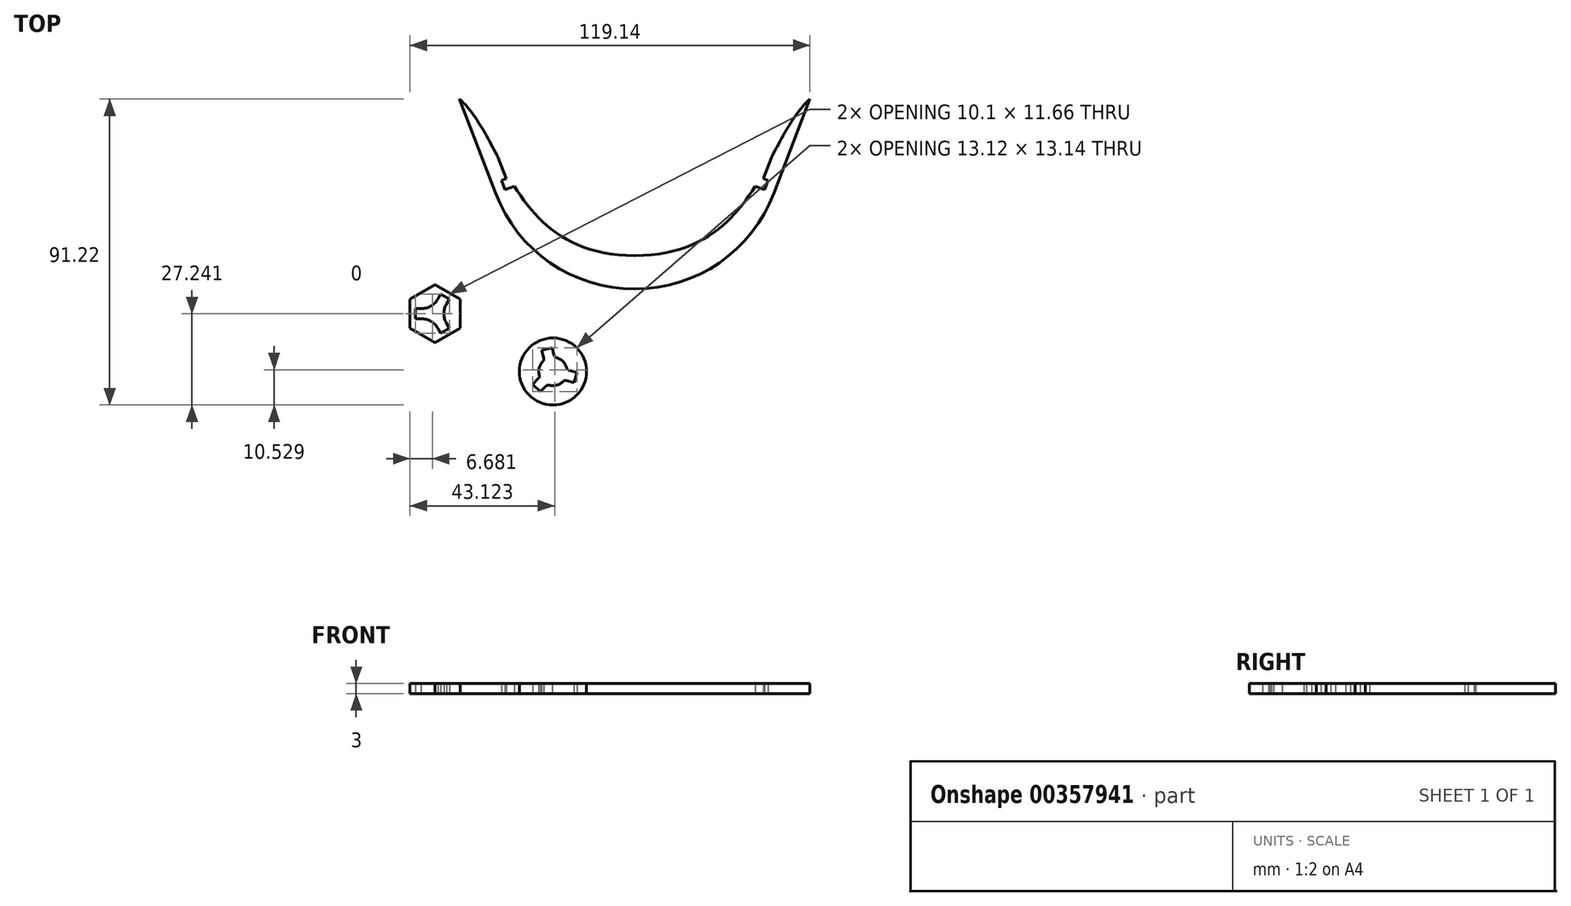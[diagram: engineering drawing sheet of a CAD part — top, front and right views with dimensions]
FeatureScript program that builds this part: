
annotation { "Feature Type Name" : "Feature", "Feature Type Description" : "" }
export const myFeature = defineFeature(function(context is Context, id is Id, definition is map)
    precondition{}
    {
        {
            var Q0;
            Q0=qCreatedBy(makeId("Top.planeOp"),FACE);
            var sketch = newSketch(context, id + "F0", { "sketchPlane" : qUnion([Q0])});
            skLineSegment(sketch, "E0", {"start": v(-52.2, 46.65) * mm, "end": v(0, -90) * mm});
            skLineSegment(sketch, "E1", {"start": v(0, -90) * mm, "end": v(0, -10) * mm});
            skLineSegment(sketch, "E2", {"start": v(-52.2, 46.65) * mm, "end": v(-43.66, 39.02) * mm, "construction": true});
            skLineSegment(sketch, "E3", {"start": v(-41.46, 18.55) * mm, "end": v(-41.46, 18.55) * mm});
            skArc(sketch, "E4", {"start": v(-41.46, 18.55) * mm, "mid": v(-25.17, -2.17) * mm, "end": v(0, -10) * mm});
            skLineSegment(sketch, "E5", {"start": v(0, -10) * mm, "end": v(0, 0) * mm});
            skLineSegment(sketch, "E6", {"start": v(-41.46, 18.55) * mm, "end": v(-36.56, 20.42) * mm, "construction": true});
            skLineSegment(sketch, "E7", {"start": v(-43.66, 39.02) * mm, "end": v(-36.56, 20.42) * mm, "construction": true});
            skLineSegment(sketch, "E8.bottom", {"start": v(-37.26, 20.15) * mm, "end": v(-40.82, 29.5) * mm});
            skLineSegment(sketch, "E8.top", {"start": v(-35.86, 20.69) * mm, "end": v(-39.42, 30.03) * mm});
            skLineSegment(sketch, "E8.left", {"start": v(-37.26, 20.15) * mm, "end": v(-35.86, 20.69) * mm});
            skLineSegment(sketch, "E8.right", {"start": v(-40.82, 29.5) * mm, "end": v(-39.42, 30.03) * mm});
            skPoint(sketch, "E8.middle", {"position": v(-38.34, 25.09) * mm});
            skLineSegment(sketch, "E9", {"start": v(-37.26, 20.15) * mm, "end": v(-38.66, 19.62) * mm});
            skLineSegment(sketch, "E10", {"start": v(-38.66, 19.62) * mm, "end": v(-39.73, 22.42) * mm});
            skLineSegment(sketch, "E11", {"start": v(-39.73, 22.42) * mm, "end": v(-38.33, 22.95) * mm});
            skFitSpline(sketch, "E12", {"points": [v(-52.2, 46.65) * mm, v(0, 0) * mm], "startDerivative": vector(41.8, -37.36) * mm, "endDerivative": vector(109.39, 0) * mm});
            skLineSegment(sketch, "E13", {"start": v(-36.46, 0) * mm, "end": v(0, 0) * mm, "construction": true});
            skLineSegment(sketch, "E14", {"start": v(-38.26, 34.2) * mm, "end": v(0, 0) * mm, "construction": true});
            skLineSegment(sketch, "E15", {"start": v(-0.08, -0.02) * mm, "end": v(-2.19, 3.07) * mm});
            skSolve(sketch);
        }
        {
            var Q0;
            {var subQ6=sQuery(id+"F0.wireOp",EDGE,"E4");Q0=makeQuery(id+"F0.imprint","IMPRINT",FACE,{"disambiguationData":[TD([[makeQuery(id+"F0.imprint","IMPRINT",EDGE,{"derivedFrom":subQ6}),1.0]])]});}
            extrude(context, id + "F1", {"entities" : qUnion([Q0]), "depth" : 3 * mm});
        }
        {
            var Q0;
            Q0=makeQuery(id+"F1.opExtrude","SWEPT_EDGE",EDGE,{"disambiguationData":[OSD([sQuery(id+"F0.wireOp",EDGE,"E8.bottom"),sQuery(id+"F0.wireOp",EDGE,"E8.right"),sQuery(id+"F0.wireOp",EDGE,"E12")])]});
            fillet(context, id + "F2", {"entities" : qUnion([Q0]), "radius" : 6 * mm, "tangentPropagation" : true, "allowEdgeOverflow" : false});
        }
        {
            var Q0;
            Q0=makeQuery(id+"F1.opExtrude","SWEPT_BODY",BODY,{"disambiguationData":[OSD([sQuery(id+"F0.wireOp",EDGE,"E0"),sQuery(id+"F0.wireOp",EDGE,"E4"),sQuery(id+"F0.wireOp",EDGE,"E5"),sQuery(id+"F0.wireOp",EDGE,"E8.bottom"),sQuery(id+"F0.wireOp",EDGE,"E8.left"),sQuery(id+"F0.wireOp",EDGE,"E9"),sQuery(id+"F0.wireOp",EDGE,"E10"),sQuery(id+"F0.wireOp",EDGE,"E11"),sQuery(id+"F0.wireOp",EDGE,"E12")])]});
            var Q1;
            Q1=makeQuery(id+"F1.opExtrude","SWEPT_FACE",FACE,{"disambiguationData":[OSD([sQuery(id+"F0.wireOp",EDGE,"E5")])]});
            mirror(context, id + "F3", {"operationType" : NewBodyOperationType.ADD, "entities" : qUnion([Q0]), "mirrorPlane" : qUnion([Q1])});
        }
        {
            var Q0;
            Q0=qCreatedBy(makeId("Top.planeOp"),FACE);
            var sketch = newSketch(context, id + "F4", { "sketchPlane" : qUnion([Q0])});
            skCircle(sketch, "E16", {"center": v(-59.45, -17.33) * mm, "radius": 7.5 * mm, "construction": true});
            skLineSegment(sketch, "E17.0", {"start": v(-59.45, -8.67) * mm, "end": v(-51.95, -13) * mm});
            skLineSegment(sketch, "E17.1", {"start": v(-51.95, -13) * mm, "end": v(-51.95, -21.66) * mm});
            skLineSegment(sketch, "E17.2", {"start": v(-51.95, -21.66) * mm, "end": v(-59.45, -25.99) * mm});
            skLineSegment(sketch, "E17.3", {"start": v(-59.45, -25.99) * mm, "end": v(-66.95, -21.66) * mm});
            skLineSegment(sketch, "E17.4", {"start": v(-66.95, -21.66) * mm, "end": v(-66.95, -13) * mm});
            skLineSegment(sketch, "E17.5", {"start": v(-66.95, -13) * mm, "end": v(-59.45, -8.67) * mm});
            skPoint(sketch, "E17.0.midPoint", {"position": v(-55.7, -10.83) * mm});
            skCircle(sketch, "E18.cCircle", {"center": v(-59.45, -17.33) * mm, "radius": 2.6 * mm, "construction": true});
            skLineSegment(sketch, "E18.0", {"start": v(-56.85, -15.83) * mm, "end": v(-56.85, -18.83) * mm, "construction": true});
            skLineSegment(sketch, "E18.1", {"start": v(-56.85, -18.83) * mm, "end": v(-59.45, -20.33) * mm, "construction": true});
            skLineSegment(sketch, "E18.2", {"start": v(-59.45, -20.33) * mm, "end": v(-62.05, -18.83) * mm, "construction": true});
            skLineSegment(sketch, "E18.3", {"start": v(-62.05, -18.83) * mm, "end": v(-62.05, -15.83) * mm, "construction": true});
            skLineSegment(sketch, "E18.4", {"start": v(-62.05, -15.83) * mm, "end": v(-59.45, -14.33) * mm, "construction": true});
            skLineSegment(sketch, "E18.5", {"start": v(-59.45, -14.33) * mm, "end": v(-56.85, -15.83) * mm, "construction": true});
            skPoint(sketch, "E18.0.midPoint", {"position": v(-56.85, -17.33) * mm});
            skLineSegment(sketch, "E19", {"start": v(-58.64, -12.91) * mm, "end": v(-57.82, -11.5) * mm});
            skLineSegment(sketch, "E20", {"start": v(-56.04, -14.41) * mm, "end": v(-55.22, -13) * mm});
            skLineSegment(sketch, "E21", {"start": v(-55.22, -13) * mm, "end": v(-57.82, -11.5) * mm});
            skLineSegment(sketch, "E22.1.0", {"start": v(-63.68, -18.83) * mm, "end": v(-65.32, -18.83) * mm});
            skLineSegment(sketch, "E22.1.1", {"start": v(-65.32, -15.83) * mm, "end": v(-65.32, -18.83) * mm});
            skLineSegment(sketch, "E22.1.2", {"start": v(-63.68, -15.83) * mm, "end": v(-65.32, -15.83) * mm});
            skLineSegment(sketch, "E22.2.0", {"start": v(-56.04, -20.24) * mm, "end": v(-55.22, -21.66) * mm});
            skLineSegment(sketch, "E22.2.1", {"start": v(-57.82, -23.16) * mm, "end": v(-55.22, -21.66) * mm});
            skLineSegment(sketch, "E22.2.2", {"start": v(-58.64, -21.74) * mm, "end": v(-57.82, -23.16) * mm});
            skArc(sketch, "E23", {"start": v(-63.68, -15.83) * mm, "mid": v(-60.75, -15.08) * mm, "end": v(-58.64, -12.91) * mm});
            skPoint(sketch, "E24.orphan", {"position": v(-62.05, -15.83) * mm});
            skArc(sketch, "E25", {"start": v(-58.64, -21.74) * mm, "mid": v(-60.75, -19.58) * mm, "end": v(-63.68, -18.83) * mm});
            skPoint(sketch, "E26.orphan", {"position": v(-59.45, -20.33) * mm});
            skPoint(sketch, "E27.orphan", {"position": v(-62.05, -18.83) * mm});
            skArc(sketch, "E28", {"start": v(-56.04, -14.41) * mm, "mid": v(-56.85, -17.33) * mm, "end": v(-56.04, -20.24) * mm});
            skPoint(sketch, "E29.orphan", {"position": v(-56.85, -18.83) * mm});
            skLineSegment(sketch, "E30", {"start": v(-57.82, -11.5) * mm, "end": v(-60.32, -15.83) * mm, "construction": true});
            skLineSegment(sketch, "E31", {"start": v(-60.32, -15.83) * mm, "end": v(-65.32, -15.83) * mm, "construction": true});
            skLineSegment(sketch, "E32", {"start": v(-65.32, -18.83) * mm, "end": v(-60.32, -18.83) * mm, "construction": true});
            skLineSegment(sketch, "E33", {"start": v(-60.32, -18.83) * mm, "end": v(-57.82, -23.16) * mm, "construction": true});
            skLineSegment(sketch, "E34", {"start": v(-55.22, -21.66) * mm, "end": v(-57.72, -17.33) * mm, "construction": true});
            skLineSegment(sketch, "E35", {"start": v(-57.72, -17.33) * mm, "end": v(-55.22, -13) * mm, "construction": true});
            skLineSegment(sketch, "E36", {"start": v(-60.32, -15.83) * mm, "end": v(-57.72, -17.33) * mm, "construction": true});
            skLineSegment(sketch, "E37", {"start": v(-60.32, -15.83) * mm, "end": v(-60.32, -18.83) * mm});
            skLineSegment(sketch, "E38", {"start": v(-60.32, -18.83) * mm, "end": v(-57.72, -17.33) * mm});
            skSolve(sketch);
        }
        {
            var Q0;
            Q0 = qSketchRegion(id + "F4", true);
            extrude(context, id + "F5", {"entities" : qUnion([Q0]), "depth" : 3 * mm});
        }
        {
            var Q0;
            Q0=qCreatedBy(makeId("Top.planeOp"),FACE);
            var sketch = newSketch(context, id + "F6", { "sketchPlane" : qUnion([Q0])});
            skCircle(sketch, "E39.cCircle", {"center": v(-24.37, -34.57) * mm, "radius": 6.92 * mm, "construction": true});
            skLineSegment(sketch, "E39.0", {"start": v(-16.65, -32.49) * mm, "end": v(-18.7, -40.21) * mm});
            skLineSegment(sketch, "E39.1", {"start": v(-18.7, -40.21) * mm, "end": v(-26.42, -42.3) * mm});
            skLineSegment(sketch, "E39.2", {"start": v(-26.42, -42.3) * mm, "end": v(-32.09, -36.66) * mm});
            skLineSegment(sketch, "E39.3", {"start": v(-32.09, -36.66) * mm, "end": v(-30.04, -28.93) * mm});
            skLineSegment(sketch, "E39.4", {"start": v(-30.04, -28.93) * mm, "end": v(-22.32, -26.85) * mm});
            skLineSegment(sketch, "E39.5", {"start": v(-22.32, -26.85) * mm, "end": v(-16.65, -32.49) * mm});
            skPoint(sketch, "E39.0.midPoint", {"position": v(-17.68, -36.35) * mm});
            skLineSegment(sketch, "E40", {"start": v(-17.27, -34.8) * mm, "end": v(-20.17, -34.03) * mm});
            skLineSegment(sketch, "E41", {"start": v(-23.85, -30.37) * mm, "end": v(-24.63, -27.47) * mm});
            skLineSegment(sketch, "E42", {"start": v(-27.72, -28.3) * mm, "end": v(-26.94, -31.2) * mm});
            skLineSegment(sketch, "E43", {"start": v(-28.27, -36.23) * mm, "end": v(-30.39, -38.35) * mm});
            skLineSegment(sketch, "E44", {"start": v(-28.12, -40.61) * mm, "end": v(-26, -38.48) * mm});
            skLineSegment(sketch, "E45", {"start": v(-20.99, -37.13) * mm, "end": v(-18.09, -37.9) * mm});
            skLineSegment(sketch, "E46", {"start": v(-26.16, -34.1) * mm, "end": v(-23.07, -33.26) * mm, "construction": true});
            skArc(sketch, "E47", {"start": v(-26, -38.48) * mm, "mid": v(-23.26, -38.66) * mm, "end": v(-20.99, -37.13) * mm});
            skLineSegment(sketch, "E48", {"start": v(-20.17, -34.03) * mm, "end": v(-20.99, -37.13) * mm, "construction": true});
            skArc(sketch, "E49.trimOffspring", {"start": v(-20.17, -34.03) * mm, "mid": v(-21.38, -31.57) * mm, "end": v(-23.85, -30.37) * mm});
            skArc(sketch, "E50.trimOffspring", {"start": v(-26.94, -31.2) * mm, "mid": v(-28.47, -33.49) * mm, "end": v(-28.27, -36.23) * mm});
            skCircle(sketch, "E51", {"center": v(-24.37, -34.57) * mm, "radius": 10 * mm});
            skSolve(sketch);
        }
        {
            var Q0;
            {var subQ7=sQuery(id+"F6.wireOp",EDGE,"E39.1");Q0=makeQuery(id+"F6.imprint","IMPRINT",FACE,{"disambiguationData":[TD([[makeQuery(id+"F6.imprint","IMPRINT",EDGE,{"derivedFrom":subQ7}),1.0]])]});}
            var Q1;
            {var subQ2=sQuery(id+"F6.wireOp",EDGE,"E39.3");Q1=makeQuery(id+"F6.imprint","IMPRINT",FACE,{"disambiguationData":[TD([[makeQuery(id+"F6.imprint","IMPRINT",EDGE,{"derivedFrom":subQ2}),-1.0]])]});}
            var Q2;
            {var subQ1=sQuery(id+"F6.wireOp",EDGE,"E39.5");Q2=makeQuery(id+"F6.imprint","IMPRINT",FACE,{"disambiguationData":[TD([[makeQuery(id+"F6.imprint","IMPRINT",EDGE,{"derivedFrom":subQ1}),-1.0]])]});}
            var Q3;
            {var subQ2=sQuery(id+"F6.wireOp",EDGE,"E39.1");Q3=makeQuery(id+"F6.imprint","IMPRINT",FACE,{"disambiguationData":[TD([[makeQuery(id+"F6.imprint","IMPRINT",EDGE,{"derivedFrom":subQ2}),-1.0]])]});}
            extrude(context, id + "F7", {"entities" : qUnion([Q0, Q1, Q2, Q3]), "depth" : 3 * mm});
        }
        {
            var Q0;
            Q0=makeQuery(id+"F7.opExtrude","SWEPT_EDGE",EDGE,{"disambiguationData":[OSD([sQuery(id+"F6.wireOp",EDGE,"E40"),sQuery(id+"F6.wireOp",EDGE,"E49.trimOffspring")])]});
            var Q1;
            Q1=makeQuery(id+"F7.opExtrude","SWEPT_EDGE",EDGE,{"disambiguationData":[OSD([sQuery(id+"F6.wireOp",EDGE,"E41"),sQuery(id+"F6.wireOp",EDGE,"E49.trimOffspring")])]});
            var Q2;
            Q2=makeQuery(id+"F7.opExtrude","SWEPT_EDGE",EDGE,{"disambiguationData":[OSD([sQuery(id+"F6.wireOp",EDGE,"E42"),sQuery(id+"F6.wireOp",EDGE,"E50.trimOffspring")])]});
            var Q3;
            Q3=makeQuery(id+"F7.opExtrude","SWEPT_EDGE",EDGE,{"disambiguationData":[OSD([sQuery(id+"F6.wireOp",EDGE,"E43"),sQuery(id+"F6.wireOp",EDGE,"E50.trimOffspring")])]});
            var Q4;
            Q4=makeQuery(id+"F7.opExtrude","SWEPT_EDGE",EDGE,{"disambiguationData":[OSD([sQuery(id+"F6.wireOp",EDGE,"E44"),sQuery(id+"F6.wireOp",EDGE,"E47")])]});
            var Q5;
            Q5=makeQuery(id+"F7.opExtrude","SWEPT_EDGE",EDGE,{"disambiguationData":[OSD([sQuery(id+"F6.wireOp",EDGE,"E45"),sQuery(id+"F6.wireOp",EDGE,"E47")])]});
            fillet(context, id + "F8", {"entities" : qUnion([Q0, Q1, Q2, Q3, Q4, Q5]), "radius" : 1 * mm, "tangentPropagation" : true, "allowEdgeOverflow" : false});
        }
    });
